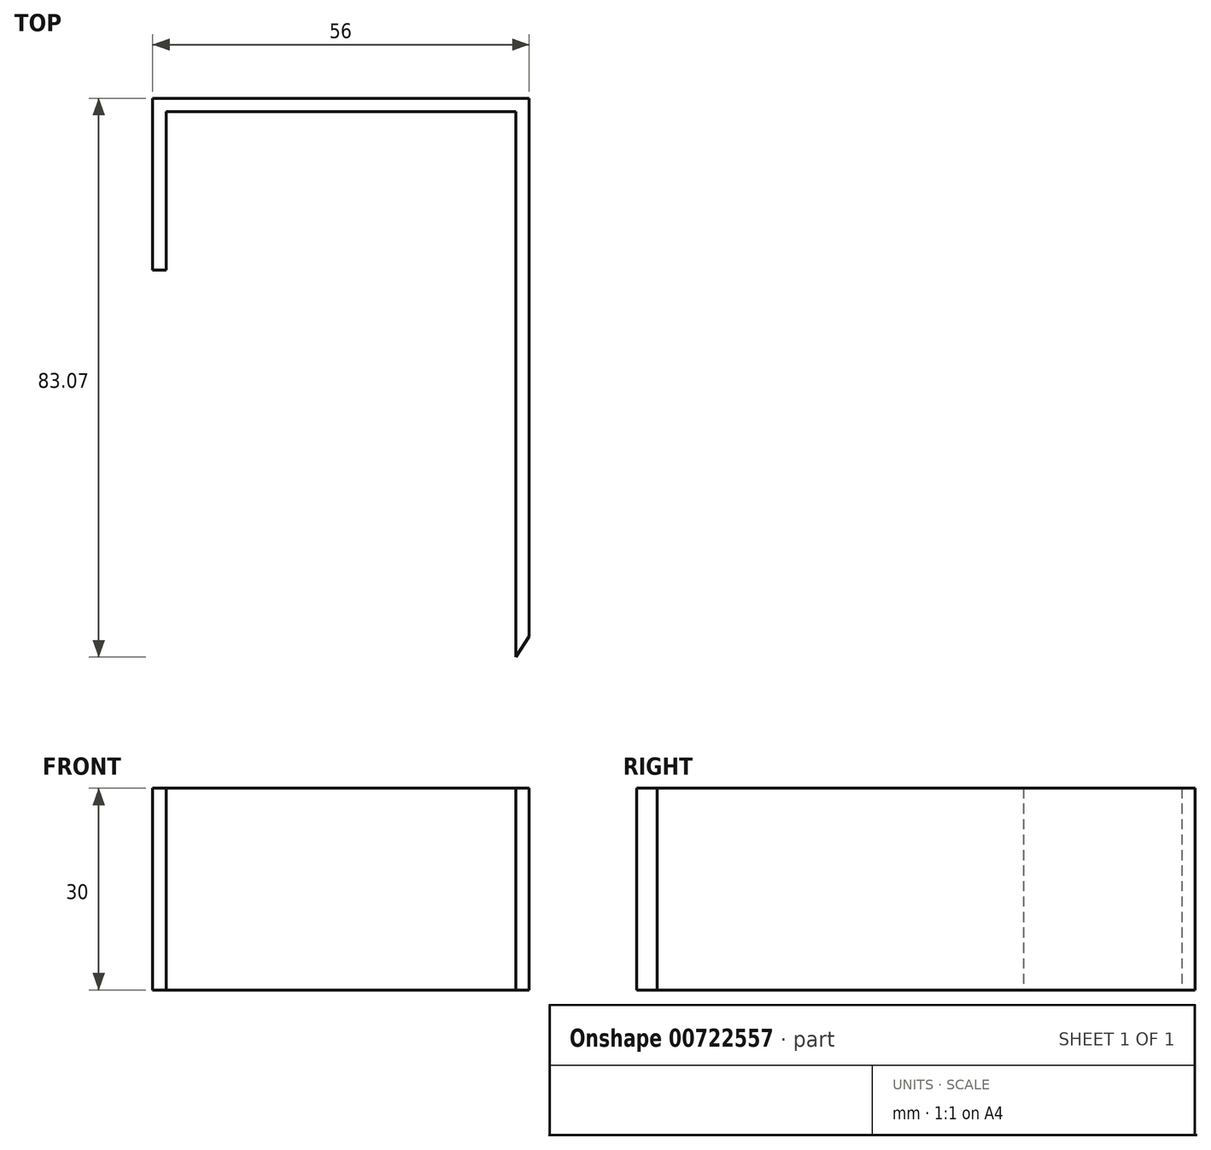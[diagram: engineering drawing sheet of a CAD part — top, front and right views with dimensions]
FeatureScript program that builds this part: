
annotation { "Feature Type Name" : "Feature", "Feature Type Description" : "" }
export const myFeature = defineFeature(function(context is Context, id is Id, definition is map)
    precondition{}
    {
        {
            var Q0;
            Q0=qCreatedBy(makeId("Top.planeOp"),FACE);
            var sketch = newSketch(context, id + "F0", { "sketchPlane" : qUnion([Q0])});
            skLineSegment(sketch, "E0", {"start": v(-22.32, 0) * mm, "end": v(-22.32, 23.56) * mm});
            skLineSegment(sketch, "E1", {"start": v(-22.32, 23.56) * mm, "end": v(29.68, 23.56) * mm});
            skLineSegment(sketch, "E2", {"start": v(29.68, 23.56) * mm, "end": v(29.68, -57.5) * mm});
            skLineSegment(sketch, "E3", {"start": v(31.68, -54.44) * mm, "end": v(31.68, 25.56) * mm});
            skLineSegment(sketch, "E4", {"start": v(31.68, 25.56) * mm, "end": v(-24.32, 25.56) * mm});
            skLineSegment(sketch, "E5", {"start": v(-24.32, 25.56) * mm, "end": v(-24.32, 0) * mm});
            skLineSegment(sketch, "E6", {"start": v(-24.32, 0) * mm, "end": v(-22.32, 0) * mm});
            skPoint(sketch, "E7", {"position": v(0, 25.56) * mm});
            skPoint(sketch, "E8", {"position": v(0, 23.56) * mm});
            skPoint(sketch, "E9", {"position": v(29.68, 0) * mm});
            skPoint(sketch, "E10", {"position": v(31.68, 0) * mm});
            skLineSegment(sketch, "E11", {"start": v(29.68, -57.5) * mm, "end": v(31.68, -54.44) * mm});
            skSolve(sketch);
        }
        {
            var Q0;
            Q0=makeQuery(id+"F0.imprint","IMPRINT",FACE,{"disambiguationData":[TD([[makeQuery(id+"F0.imprint","IMPRINT",EDGE,{"derivedFrom":sQuery(id+"F0.wireOp",EDGE,"E0")}),1.0]])]});
            extrude(context, id + "F1", {"entities" : qUnion([Q0]), "depth" : 30 * mm, "offsetDistance" : 25 * mm});
        }
    });
